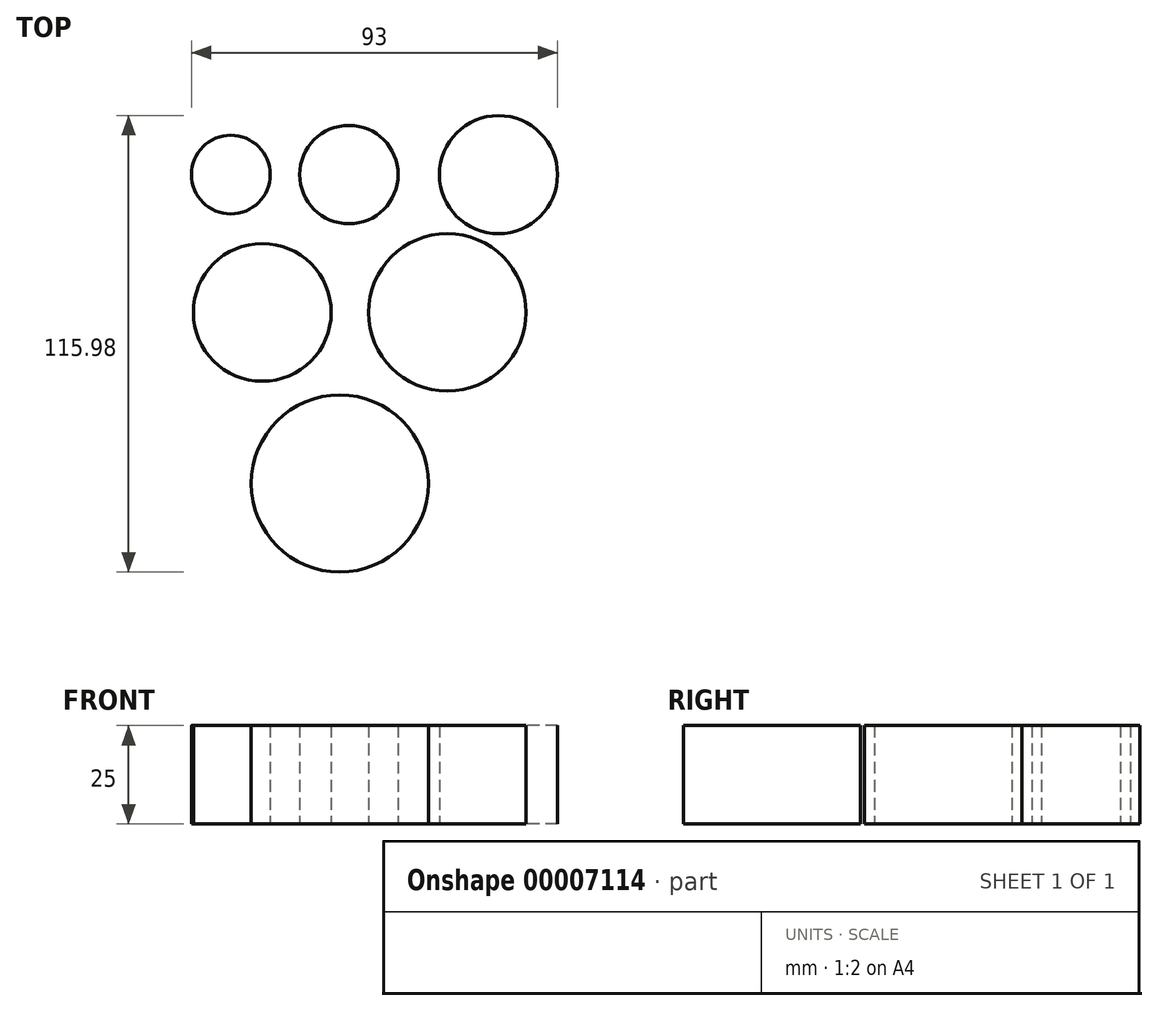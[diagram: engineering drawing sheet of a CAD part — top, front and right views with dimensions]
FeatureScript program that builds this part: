
annotation { "Feature Type Name" : "Feature", "Feature Type Description" : "" }
export const myFeature = defineFeature(function(context is Context, id is Id, definition is map)
    precondition{}
    {
        {
            var Q0;
            Q0=qCreatedBy(makeId("Top.planeOp"),FACE);
            var sketch = newSketch(context, id + "F0", { "sketchPlane" : qUnion([Q0])});
            skLineSegment(sketch, "E0.rect.bottom", {"start": v(-50, 60) * mm, "end": v(50, 60) * mm});
            skLineSegment(sketch, "E0.rect.top", {"start": v(-50, -60) * mm, "end": v(50, -60) * mm});
            skLineSegment(sketch, "E0.rect.left", {"start": v(-50, 60) * mm, "end": v(-50, -60) * mm});
            skLineSegment(sketch, "E0.rect.right", {"start": v(50, 60) * mm, "end": v(50, -60) * mm});
            skPoint(sketch, "E0.rect.middle", {"position": v(0, 0) * mm});
            skCircle(sketch, "E1", {"center": v(-38, 43) * mm, "radius": 10 * mm});
            skCircle(sketch, "E2", {"center": v(-8, 43) * mm, "radius": 12.5 * mm});
            skCircle(sketch, "E3", {"center": v(30, 43) * mm, "radius": 15 * mm});
            skCircle(sketch, "E4", {"center": v(-30, 8) * mm, "radius": 17.5 * mm});
            skCircle(sketch, "E5", {"center": v(17, 8) * mm, "radius": 20 * mm});
            skCircle(sketch, "E6", {"center": v(-10.32, -35.48) * mm, "radius": 22.5 * mm});
            skSolve(sketch);
        }
        {
            var Q0;
            Q0=makeQuery(id+"F0.imprint","IMPRINT",FACE,{"disambiguationData":[TD([[makeQuery(id+"F0.imprint","IMPRINT",EDGE,{"derivedFrom":sQuery(id+"F0.wireOp",EDGE,"E1")}),1.0]])]});
            var Q1;
            Q1=makeQuery(id+"F0.imprint","IMPRINT",FACE,{"disambiguationData":[TD([[makeQuery(id+"F0.imprint","IMPRINT",EDGE,{"derivedFrom":sQuery(id+"F0.wireOp",EDGE,"E2")}),1.0]])]});
            var Q2;
            Q2=makeQuery(id+"F0.imprint","IMPRINT",FACE,{"disambiguationData":[TD([[makeQuery(id+"F0.imprint","IMPRINT",EDGE,{"derivedFrom":sQuery(id+"F0.wireOp",EDGE,"E3")}),1.0]])]});
            var Q3;
            Q3=makeQuery(id+"F0.imprint","IMPRINT",FACE,{"disambiguationData":[TD([[makeQuery(id+"F0.imprint","IMPRINT",EDGE,{"derivedFrom":sQuery(id+"F0.wireOp",EDGE,"E5")}),1.0]])]});
            var Q4;
            Q4=makeQuery(id+"F0.imprint","IMPRINT",FACE,{"disambiguationData":[TD([[makeQuery(id+"F0.imprint","IMPRINT",EDGE,{"derivedFrom":sQuery(id+"F0.wireOp",EDGE,"E6")}),1.0]])]});
            var Q5;
            Q5=makeQuery(id+"F0.imprint","IMPRINT",FACE,{"disambiguationData":[TD([[makeQuery(id+"F0.imprint","IMPRINT",EDGE,{"derivedFrom":sQuery(id+"F0.wireOp",EDGE,"E4")}),1.0]])]});
            extrude(context, id + "F1", {"entities" : qUnion([Q0, Q1, Q2, Q3, Q4, Q5]), "depth" : 25 * mm});
        }
    });
